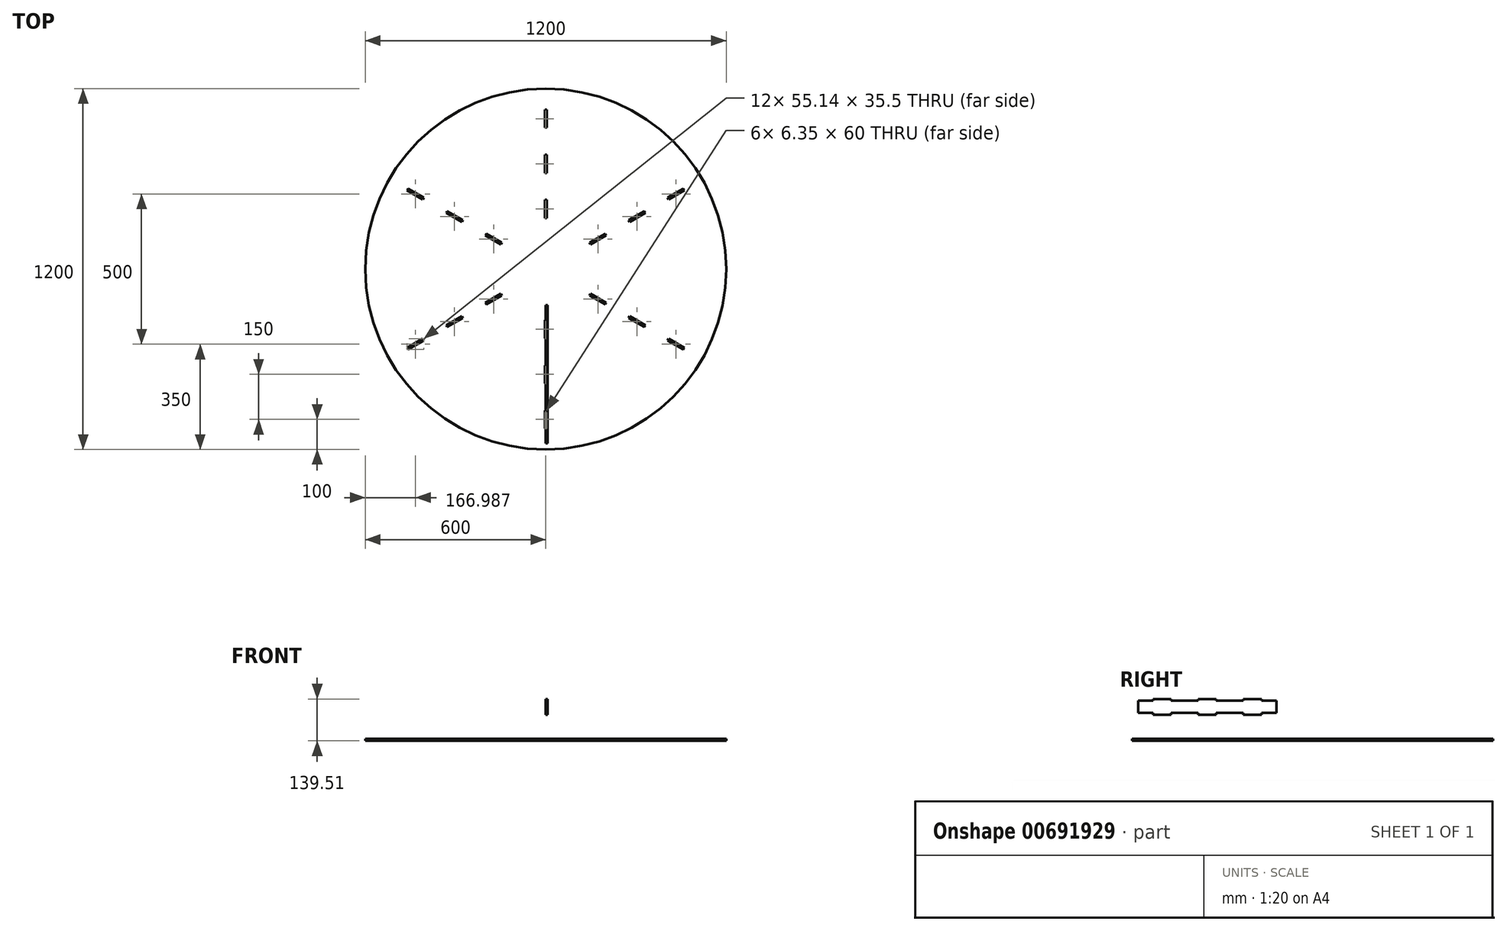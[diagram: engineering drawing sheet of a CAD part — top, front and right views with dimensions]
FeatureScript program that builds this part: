
annotation { "Feature Type Name" : "Feature", "Feature Type Description" : "" }
export const myFeature = defineFeature(function(context is Context, id is Id, definition is map)
    precondition{}
    {
        {
            var Q0;
            Q0=qCreatedBy(makeId("Top.planeOp"),FACE);
            var sketch = newSketch(context, id + "F0", { "sketchPlane" : qUnion([Q0])});
            skCircle(sketch, "E0", {"center": v(0, 0) * mm, "radius": 600 * mm});
            skSolve(sketch);
        }
        {
            var Q0;
            Q0=qCreatedBy(makeId("Top.planeOp"),FACE);
            var sketch = newSketch(context, id + "F1", { "sketchPlane" : qUnion([Q0])});
            skLineSegment(sketch, "E1.bottom", {"start": v(3.17, 230) * mm, "end": v(-3.18, 230) * mm});
            skLineSegment(sketch, "E1.top", {"start": v(3.17, 170) * mm, "end": v(-3.18, 170) * mm});
            skLineSegment(sketch, "E1.left", {"start": v(3.18, 230) * mm, "end": v(3.18, 170) * mm});
            skLineSegment(sketch, "E1.right", {"start": v(-3.17, 230) * mm, "end": v(-3.17, 170) * mm});
            skPoint(sketch, "E1.middle", {"position": v(0, 200) * mm});
            skPoint(sketch, "E2.middle", {"position": v(0, 350) * mm});
            skLineSegment(sketch, "E3", {"start": v(0, 0) * mm, "end": v(0, 730.46) * mm, "construction": true});
            skLineSegment(sketch, "E4.bottom", {"start": v(3.17, 320) * mm, "end": v(-3.18, 320) * mm});
            skLineSegment(sketch, "E4.top", {"start": v(3.17, 380) * mm, "end": v(-3.18, 380) * mm});
            skLineSegment(sketch, "E4.left", {"start": v(3.17, 320) * mm, "end": v(3.17, 380) * mm});
            skLineSegment(sketch, "E4.right", {"start": v(-3.18, 320) * mm, "end": v(-3.18, 380) * mm});
            skLineSegment(sketch, "E5.bottom", {"start": v(3.17, 470) * mm, "end": v(-3.18, 470) * mm});
            skLineSegment(sketch, "E5.top", {"start": v(3.17, 530) * mm, "end": v(-3.18, 530) * mm});
            skLineSegment(sketch, "E5.left", {"start": v(3.17, 470) * mm, "end": v(3.17, 530) * mm});
            skLineSegment(sketch, "E5.right", {"start": v(-3.18, 470) * mm, "end": v(-3.18, 530) * mm});
            skPoint(sketch, "E5.middle", {"position": v(0, 500) * mm});
            skPoint(sketch, "E6.1.0", {"position": v(-173.2, 100) * mm});
            skPoint(sketch, "E6.1.1", {"position": v(-303.1, 175) * mm});
            skPoint(sketch, "E6.1.2", {"position": v(-433.01, 250) * mm});
            skLineSegment(sketch, "E6.1.3", {"start": v(-408.62, 232.25) * mm, "end": v(-460.58, 262.25) * mm});
            skLineSegment(sketch, "E6.1.4", {"start": v(-405.44, 237.75) * mm, "end": v(-457.4, 267.75) * mm});
            skLineSegment(sketch, "E6.1.5", {"start": v(-200.77, 112.25) * mm, "end": v(-148.81, 82.25) * mm});
            skLineSegment(sketch, "E6.1.6", {"start": v(-197.6, 117.75) * mm, "end": v(-145.64, 87.75) * mm});
            skPoint(sketch, "E6.1.7", {"position": v(-303.1, 175) * mm});
            skLineSegment(sketch, "E6.1.8", {"start": v(-457.4, 267.75) * mm, "end": v(-460.58, 262.25) * mm});
            skLineSegment(sketch, "E6.1.9", {"start": v(-405.44, 237.75) * mm, "end": v(-408.62, 232.25) * mm});
            skLineSegment(sketch, "E6.1.10", {"start": v(-278.72, 157.25) * mm, "end": v(-330.68, 187.25) * mm});
            skLineSegment(sketch, "E6.1.11", {"start": v(-275.54, 162.75) * mm, "end": v(-327.5, 192.75) * mm});
            skLineSegment(sketch, "E6.1.12", {"start": v(-327.5, 192.75) * mm, "end": v(-330.68, 187.25) * mm});
            skLineSegment(sketch, "E6.1.13", {"start": v(-145.64, 87.75) * mm, "end": v(-148.81, 82.25) * mm});
            skLineSegment(sketch, "E6.1.14", {"start": v(-197.6, 117.75) * mm, "end": v(-200.77, 112.25) * mm});
            skLineSegment(sketch, "E6.1.15", {"start": v(-275.54, 162.75) * mm, "end": v(-278.72, 157.25) * mm});
            skPoint(sketch, "E6.2.0", {"position": v(-173.2, -100) * mm});
            skPoint(sketch, "E6.2.1", {"position": v(-303.1, -175) * mm});
            skPoint(sketch, "E6.2.2", {"position": v(-433.01, -250) * mm});
            skLineSegment(sketch, "E6.2.3", {"start": v(-405.44, -237.75) * mm, "end": v(-457.4, -267.75) * mm});
            skLineSegment(sketch, "E6.2.4", {"start": v(-408.62, -232.25) * mm, "end": v(-460.58, -262.25) * mm});
            skLineSegment(sketch, "E6.2.5", {"start": v(-197.6, -117.75) * mm, "end": v(-145.64, -87.75) * mm});
            skLineSegment(sketch, "E6.2.6", {"start": v(-200.77, -112.25) * mm, "end": v(-148.81, -82.25) * mm});
            skPoint(sketch, "E6.2.7", {"position": v(-303.1, -175) * mm});
            skLineSegment(sketch, "E6.2.8", {"start": v(-460.58, -262.25) * mm, "end": v(-457.4, -267.75) * mm});
            skLineSegment(sketch, "E6.2.9", {"start": v(-408.62, -232.25) * mm, "end": v(-405.44, -237.75) * mm});
            skLineSegment(sketch, "E6.2.10", {"start": v(-275.54, -162.75) * mm, "end": v(-327.5, -192.75) * mm});
            skLineSegment(sketch, "E6.2.11", {"start": v(-278.72, -157.25) * mm, "end": v(-330.68, -187.25) * mm});
            skLineSegment(sketch, "E6.2.12", {"start": v(-330.68, -187.25) * mm, "end": v(-327.5, -192.75) * mm});
            skLineSegment(sketch, "E6.2.13", {"start": v(-148.81, -82.25) * mm, "end": v(-145.64, -87.75) * mm});
            skLineSegment(sketch, "E6.2.14", {"start": v(-200.77, -112.25) * mm, "end": v(-197.6, -117.75) * mm});
            skLineSegment(sketch, "E6.2.15", {"start": v(-278.72, -157.25) * mm, "end": v(-275.54, -162.75) * mm});
            skPoint(sketch, "E6.3.0", {"position": v(0, -200) * mm});
            skPoint(sketch, "E6.3.1", {"position": v(0, -350) * mm});
            skPoint(sketch, "E6.3.2", {"position": v(0, -500) * mm});
            skLineSegment(sketch, "E6.3.3", {"start": v(3.17, -470) * mm, "end": v(3.17, -530) * mm});
            skLineSegment(sketch, "E6.3.4", {"start": v(-3.18, -470) * mm, "end": v(-3.18, -530) * mm});
            skLineSegment(sketch, "E6.3.5", {"start": v(3.17, -230) * mm, "end": v(3.17, -170) * mm});
            skLineSegment(sketch, "E6.3.6", {"start": v(-3.18, -230) * mm, "end": v(-3.18, -170) * mm});
            skPoint(sketch, "E6.3.7", {"position": v(0, -350) * mm});
            skLineSegment(sketch, "E6.3.8", {"start": v(-3.18, -530) * mm, "end": v(3.17, -530) * mm});
            skLineSegment(sketch, "E6.3.9", {"start": v(-3.18, -470) * mm, "end": v(3.17, -470) * mm});
            skLineSegment(sketch, "E6.3.10", {"start": v(3.17, -320) * mm, "end": v(3.17, -380) * mm});
            skLineSegment(sketch, "E6.3.11", {"start": v(-3.18, -320) * mm, "end": v(-3.18, -380) * mm});
            skLineSegment(sketch, "E6.3.12", {"start": v(-3.18, -380) * mm, "end": v(3.17, -380) * mm});
            skLineSegment(sketch, "E6.3.13", {"start": v(-3.17, -170) * mm, "end": v(3.18, -170) * mm});
            skLineSegment(sketch, "E6.3.14", {"start": v(-3.17, -230) * mm, "end": v(3.18, -230) * mm});
            skLineSegment(sketch, "E6.3.15", {"start": v(-3.18, -320) * mm, "end": v(3.17, -320) * mm});
            skPoint(sketch, "E6.4.0", {"position": v(173.2, -100) * mm});
            skPoint(sketch, "E6.4.1", {"position": v(303.1, -175) * mm});
            skPoint(sketch, "E6.4.2", {"position": v(433.01, -250) * mm});
            skLineSegment(sketch, "E6.4.3", {"start": v(408.62, -232.25) * mm, "end": v(460.58, -262.25) * mm});
            skLineSegment(sketch, "E6.4.4", {"start": v(405.44, -237.75) * mm, "end": v(457.4, -267.75) * mm});
            skLineSegment(sketch, "E6.4.5", {"start": v(200.77, -112.25) * mm, "end": v(148.81, -82.25) * mm});
            skLineSegment(sketch, "E6.4.6", {"start": v(197.6, -117.75) * mm, "end": v(145.64, -87.75) * mm});
            skPoint(sketch, "E6.4.7", {"position": v(303.1, -175) * mm});
            skLineSegment(sketch, "E6.4.8", {"start": v(457.4, -267.75) * mm, "end": v(460.58, -262.25) * mm});
            skLineSegment(sketch, "E6.4.9", {"start": v(405.44, -237.75) * mm, "end": v(408.62, -232.25) * mm});
            skLineSegment(sketch, "E6.4.10", {"start": v(278.72, -157.25) * mm, "end": v(330.68, -187.25) * mm});
            skLineSegment(sketch, "E6.4.11", {"start": v(275.54, -162.75) * mm, "end": v(327.5, -192.75) * mm});
            skLineSegment(sketch, "E6.4.12", {"start": v(327.5, -192.75) * mm, "end": v(330.68, -187.25) * mm});
            skLineSegment(sketch, "E6.4.13", {"start": v(145.64, -87.75) * mm, "end": v(148.81, -82.25) * mm});
            skLineSegment(sketch, "E6.4.14", {"start": v(197.6, -117.75) * mm, "end": v(200.77, -112.25) * mm});
            skLineSegment(sketch, "E6.4.15", {"start": v(275.54, -162.75) * mm, "end": v(278.72, -157.25) * mm});
            skPoint(sketch, "E6.5.0", {"position": v(173.2, 100) * mm});
            skPoint(sketch, "E6.5.1", {"position": v(303.1, 175) * mm});
            skPoint(sketch, "E6.5.2", {"position": v(433.01, 250) * mm});
            skLineSegment(sketch, "E6.5.3", {"start": v(405.44, 237.75) * mm, "end": v(457.4, 267.75) * mm});
            skLineSegment(sketch, "E6.5.4", {"start": v(408.62, 232.25) * mm, "end": v(460.58, 262.25) * mm});
            skLineSegment(sketch, "E6.5.5", {"start": v(197.6, 117.75) * mm, "end": v(145.64, 87.75) * mm});
            skLineSegment(sketch, "E6.5.6", {"start": v(200.77, 112.25) * mm, "end": v(148.81, 82.25) * mm});
            skPoint(sketch, "E6.5.7", {"position": v(303.1, 175) * mm});
            skLineSegment(sketch, "E6.5.8", {"start": v(460.58, 262.25) * mm, "end": v(457.4, 267.75) * mm});
            skLineSegment(sketch, "E6.5.9", {"start": v(408.62, 232.25) * mm, "end": v(405.44, 237.75) * mm});
            skLineSegment(sketch, "E6.5.10", {"start": v(275.54, 162.75) * mm, "end": v(327.5, 192.75) * mm});
            skLineSegment(sketch, "E6.5.11", {"start": v(278.72, 157.25) * mm, "end": v(330.68, 187.25) * mm});
            skLineSegment(sketch, "E6.5.12", {"start": v(330.68, 187.25) * mm, "end": v(327.5, 192.75) * mm});
            skLineSegment(sketch, "E6.5.13", {"start": v(148.81, 82.25) * mm, "end": v(145.64, 87.75) * mm});
            skLineSegment(sketch, "E6.5.14", {"start": v(200.77, 112.25) * mm, "end": v(197.6, 117.75) * mm});
            skLineSegment(sketch, "E6.5.15", {"start": v(278.72, 157.25) * mm, "end": v(275.54, 162.75) * mm});
            skPoint(sketch, "E6.center", {"position": v(0, 0) * mm});
            skSolve(sketch);
        }
        {
            var Q0;
            Q0 = qSketchRegion(id + "F0", true);
            extrude(context, id + "F2", {"entities" : qUnion([Q0]), "depth" : 6.3 * mm, "offsetDistance" : 25 * mm});
        }
        {
            var Q0;
            Q0 = qSketchRegion(id + "F1", true);
            extrude(context, id + "F3", {"entities" : qUnion([Q0]), "operationType" : NewBodyOperationType.REMOVE, "depth" : 25 * mm, "offsetDistance" : 25 * mm});
        }
        {
            var Q0;
            Q0=qCreatedBy(makeId("Right.planeOp"),FACE);
            var sketch = newSketch(context, id + "F4", { "sketchPlane" : qUnion([Q0])});
            skLineSegment(sketch, "E7", {"start": v(-22.76, 22.4) * mm, "end": v(-75.17, 22.4) * mm});
            skLineSegment(sketch, "E8", {"start": v(-75.17, 22.4) * mm, "end": v(-75.17, 5.43) * mm});
            skLineSegment(sketch, "E9", {"start": v(-75.17, 5.43) * mm, "end": v(-138.5, 5.43) * mm});
            skLineSegment(sketch, "E10", {"start": v(-138.5, 5.43) * mm, "end": v(-138.5, 21.12) * mm});
            skLineSegment(sketch, "E11", {"start": v(-138.5, 21.12) * mm, "end": v(-198.35, 21.12) * mm});
            skLineSegment(sketch, "E12", {"start": v(-198.35, 21.12) * mm, "end": v(-198.35, 6.62) * mm});
            skLineSegment(sketch, "E13", {"start": v(-198.35, 6.62) * mm, "end": v(-278.73, 6.62) * mm});
            skLineSegment(sketch, "E14", {"start": v(-278.73, 6.62) * mm, "end": v(-278.73, 23.08) * mm});
            skLineSegment(sketch, "E15", {"start": v(-278.73, 23.08) * mm, "end": v(-356.6, 23.08) * mm});
            skLineSegment(sketch, "E16", {"start": v(-356.6, 23.08) * mm, "end": v(-356.6, 9.37) * mm});
            skLineSegment(sketch, "E17", {"start": v(-356.6, 9.37) * mm, "end": v(-435.62, 9.37) * mm});
            skLineSegment(sketch, "E18", {"start": v(-435.62, 9.37) * mm, "end": v(-435.62, 25.1) * mm});
            skLineSegment(sketch, "E19", {"start": v(-40.2, 49.15) * mm, "end": v(-454.33, 49.15) * mm});
            skLineSegment(sketch, "E20", {"start": v(-454.33, 49.15) * mm, "end": v(-454.33, 25.1) * mm});
            skLineSegment(sketch, "E21", {"start": v(-454.33, 25.1) * mm, "end": v(-435.62, 25.1) * mm});
            skLineSegment(sketch, "E22.bottom", {"start": v(-580, 113.2) * mm, "end": v(-120, 113.2) * mm});
            skLineSegment(sketch, "E22.top", {"start": v(-580, 93.2) * mm, "end": v(-120, 93.2) * mm});
            skLineSegment(sketch, "E22.left", {"start": v(-580, 113.2) * mm, "end": v(-580, 93.2) * mm});
            skLineSegment(sketch, "E22.right", {"start": v(-120, 113.2) * mm, "end": v(-120, 93.2) * mm});
            skLineSegment(sketch, "E23.bottom", {"start": v(-470, 86.9) * mm, "end": v(-530, 86.9) * mm});
            skLineSegment(sketch, "E23.top", {"start": v(-470, 99.5) * mm, "end": v(-530, 99.5) * mm});
            skLineSegment(sketch, "E23.left", {"start": v(-470, 86.9) * mm, "end": v(-470, 99.5) * mm});
            skLineSegment(sketch, "E23.right", {"start": v(-530, 86.9) * mm, "end": v(-530, 99.5) * mm});
            skPoint(sketch, "E23.middle", {"position": v(-500, 93.2) * mm});
            skLineSegment(sketch, "E24.bottom", {"start": v(-320, 86.9) * mm, "end": v(-380, 86.9) * mm});
            skLineSegment(sketch, "E24.top", {"start": v(-320, 99.5) * mm, "end": v(-380, 99.5) * mm});
            skLineSegment(sketch, "E24.left", {"start": v(-320, 86.9) * mm, "end": v(-320, 99.5) * mm});
            skLineSegment(sketch, "E24.right", {"start": v(-380, 86.9) * mm, "end": v(-380, 99.5) * mm});
            skPoint(sketch, "E24.middle", {"position": v(-350, 93.2) * mm});
            skLineSegment(sketch, "E25.bottom", {"start": v(-170, 86.9) * mm, "end": v(-230, 86.9) * mm});
            skLineSegment(sketch, "E25.top", {"start": v(-170, 99.5) * mm, "end": v(-230, 99.5) * mm});
            skLineSegment(sketch, "E25.left", {"start": v(-170, 86.9) * mm, "end": v(-170, 99.5) * mm});
            skLineSegment(sketch, "E25.right", {"start": v(-230, 86.9) * mm, "end": v(-230, 99.5) * mm});
            skPoint(sketch, "E25.middle", {"position": v(-200, 93.2) * mm});
            skLineSegment(sketch, "E26.MirrorCS", {"start": v(-470, 139.5) * mm, "end": v(-470, 126.9) * mm});
            skLineSegment(sketch, "E27.MirrorCS", {"start": v(-530, 139.5) * mm, "end": v(-530, 126.9) * mm});
            skLineSegment(sketch, "E28.MirrorCS", {"start": v(-320, 139.5) * mm, "end": v(-320, 126.9) * mm});
            skLineSegment(sketch, "E29.MirrorCS", {"start": v(-380, 139.5) * mm, "end": v(-380, 126.9) * mm});
            skLineSegment(sketch, "E30.MirrorCS", {"start": v(-170, 139.5) * mm, "end": v(-170, 126.9) * mm});
            skLineSegment(sketch, "E31.MirrorCS", {"start": v(-230, 139.5) * mm, "end": v(-230, 126.9) * mm});
            skLineSegment(sketch, "E32.MirrorCS", {"start": v(-580, 133.2) * mm, "end": v(-120, 133.2) * mm});
            skPoint(sketch, "E33.MirrorP", {"position": v(-200, 133.2) * mm});
            skLineSegment(sketch, "E34.MirrorCS", {"start": v(-470, 139.5) * mm, "end": v(-530, 139.5) * mm});
            skLineSegment(sketch, "E35.MirrorCS", {"start": v(-470, 126.9) * mm, "end": v(-530, 126.9) * mm});
            skLineSegment(sketch, "E36.MirrorCS", {"start": v(-320, 139.5) * mm, "end": v(-380, 139.5) * mm});
            skLineSegment(sketch, "E37.MirrorCS", {"start": v(-320, 126.9) * mm, "end": v(-380, 126.9) * mm});
            skLineSegment(sketch, "E38.MirrorCS", {"start": v(-170, 139.5) * mm, "end": v(-230, 139.5) * mm});
            skPoint(sketch, "E39.MirrorP", {"position": v(-500, 133.2) * mm});
            skLineSegment(sketch, "E40.MirrorCS", {"start": v(-170, 126.9) * mm, "end": v(-230, 126.9) * mm});
            skPoint(sketch, "E41.MirrorP", {"position": v(-350, 133.2) * mm});
            skLineSegment(sketch, "E42.MirrorCS", {"start": v(-120, 113.2) * mm, "end": v(-120, 133.2) * mm});
            skLineSegment(sketch, "E43.MirrorCS", {"start": v(-580, 113.2) * mm, "end": v(-580, 133.2) * mm});
            skSolve(sketch);
        }
        {
            var Q0;
            Q0 = qSketchRegion(id + "F4", true);
            extrude(context, id + "F5", {"entities" : qUnion([Q0]), "depth" : 6.3 * mm, "offsetDistance" : 25 * mm});
        }
    });
